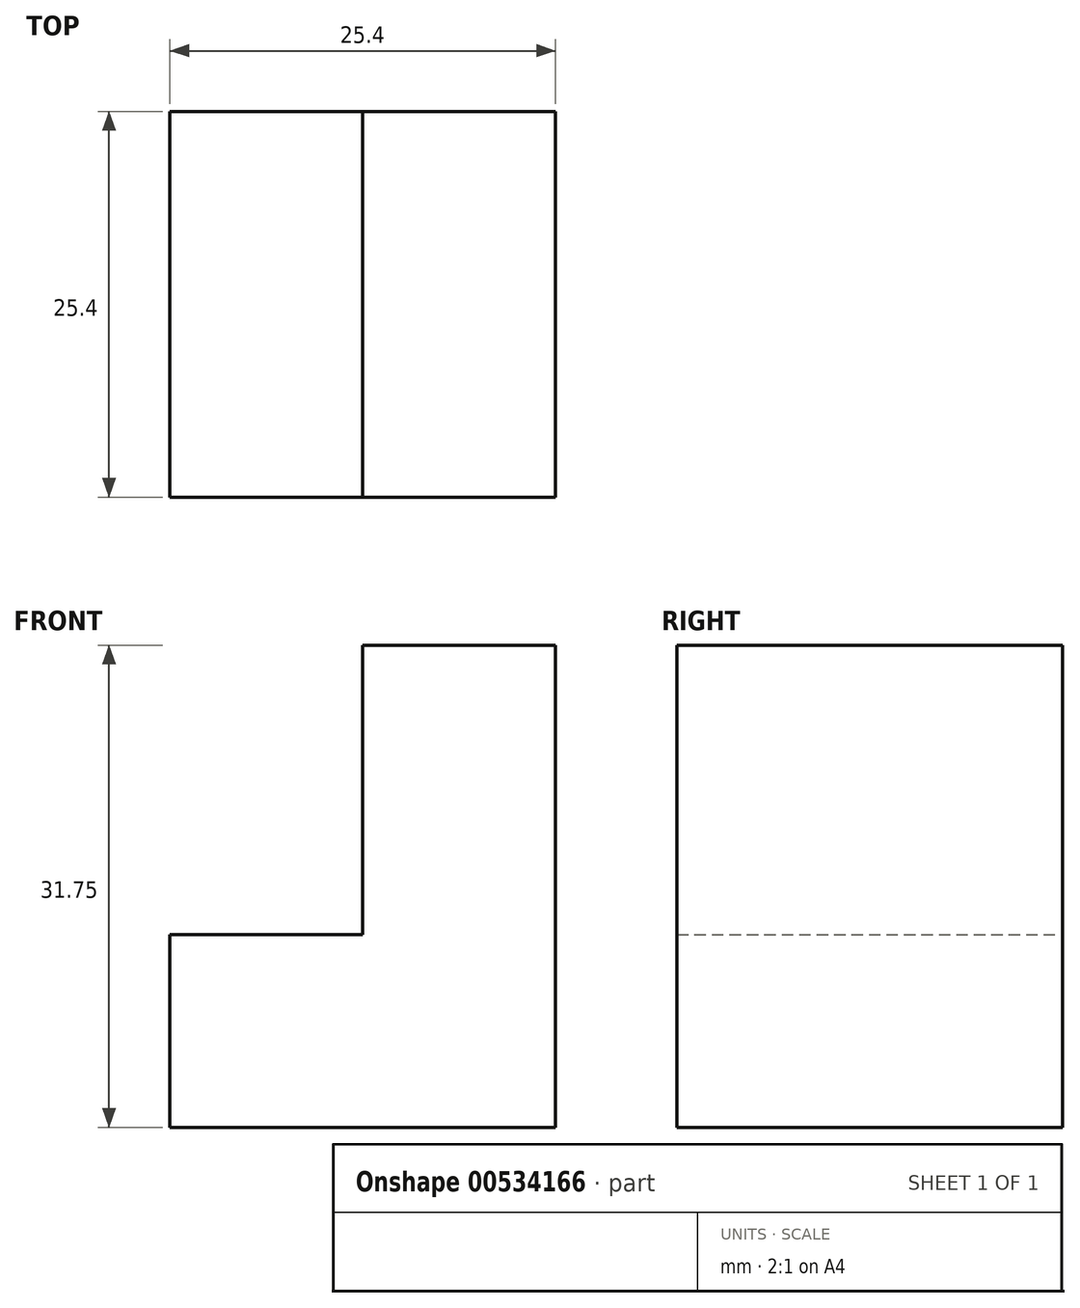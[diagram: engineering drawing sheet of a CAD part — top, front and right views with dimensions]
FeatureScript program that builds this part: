
annotation { "Feature Type Name" : "Feature", "Feature Type Description" : "" }
export const myFeature = defineFeature(function(context is Context, id is Id, definition is map)
    precondition{}
    {
        {
            var Q0;
            Q0=qCreatedBy(makeId("Front.planeOp"),FACE);
            var sketch = newSketch(context, id + "F0", { "sketchPlane" : qUnion([Q0])});
            skLineSegment(sketch, "E0", {"start": v(0, 0) * mm, "end": v(0, 31.75) * mm});
            skLineSegment(sketch, "E1", {"start": v(0, 31.75) * mm, "end": v(-12.7, 31.75) * mm});
            skLineSegment(sketch, "E2", {"start": v(-12.7, 31.75) * mm, "end": v(-12.7, 12.7) * mm});
            skLineSegment(sketch, "E3", {"start": v(-12.7, 12.7) * mm, "end": v(-25.4, 12.7) * mm});
            skLineSegment(sketch, "E4", {"start": v(-25.4, 12.7) * mm, "end": v(-25.4, 0) * mm});
            skLineSegment(sketch, "E5", {"start": v(-25.4, 0) * mm, "end": v(0, 0) * mm});
            skSolve(sketch);
        }
        {
            var Q0;
            Q0=makeQuery(id+"F0.imprint","IMPRINT",FACE,{"disambiguationData":[TD([[makeQuery(id+"F0.imprint","IMPRINT",EDGE,{"derivedFrom":sQuery(id+"F0.wireOp",EDGE,"E0")}),1.0]])]});
            extrude(context, id + "F1", {"entities" : qUnion([Q0]), "depth" : 25.4 * mm, "offsetDistance" : 25.4 * mm});
        }
    });
